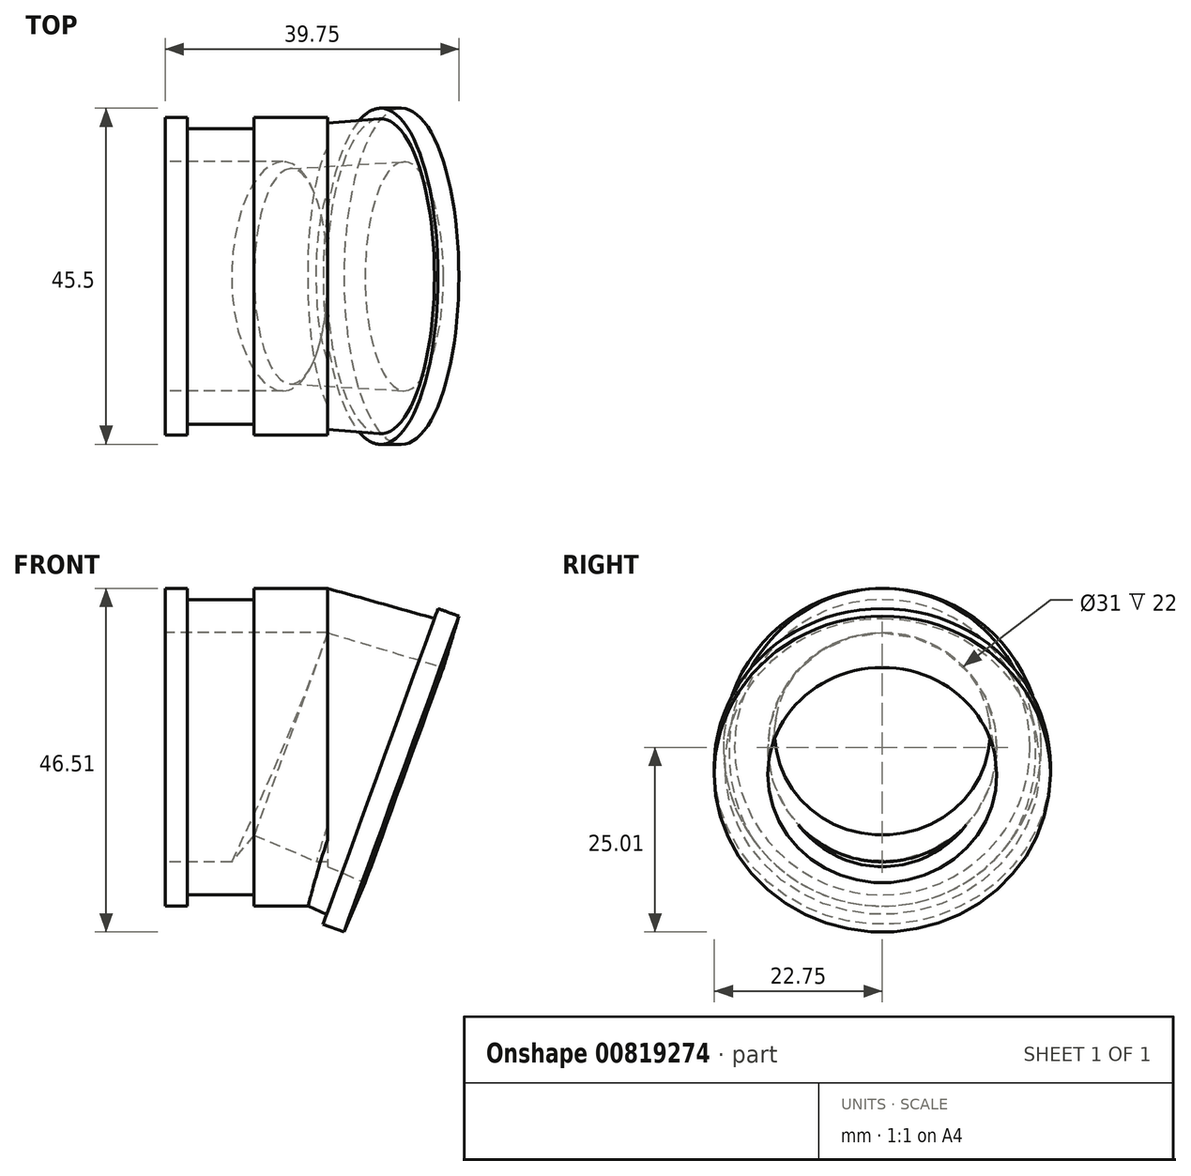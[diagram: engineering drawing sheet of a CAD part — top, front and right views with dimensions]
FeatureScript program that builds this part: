
annotation { "Feature Type Name" : "Feature", "Feature Type Description" : "" }
export const myFeature = defineFeature(function(context is Context, id is Id, definition is map)
    precondition{}
    {
        {
            var Q0;
            Q0=qCreatedBy(makeId("Front.planeOp"),FACE);
            var sketch = newSketch(context, id + "F0", { "sketchPlane" : qUnion([Q0])});
            skLineSegment(sketch, "E0", {"start": v(-22, 15.5) * mm, "end": v(-22, 21.5) * mm});
            skLineSegment(sketch, "E1", {"start": v(-22, 21.5) * mm, "end": v(-19, 21.5) * mm});
            skLineSegment(sketch, "E2", {"start": v(-19, 21.5) * mm, "end": v(-19, 20) * mm});
            skLineSegment(sketch, "E3", {"start": v(-19, 20) * mm, "end": v(-10, 20) * mm});
            skLineSegment(sketch, "E4", {"start": v(-10, 20) * mm, "end": v(-10, 21.5) * mm});
            skLineSegment(sketch, "E5", {"start": v(-10, 21.5) * mm, "end": v(0, 21.5) * mm});
            skLineSegment(sketch, "E6", {"start": v(0, 15.5) * mm, "end": v(-22, 15.5) * mm});
            skLineSegment(sketch, "E7", {"start": v(-22, 0) * mm, "end": v(0, 0) * mm, "construction": true});
            skLineSegment(sketch, "E8", {"start": v(0, 21.5) * mm, "end": v(0, 15.5) * mm});
            skSolve(sketch);
        }
        {
            var Q0;
            Q0=makeQuery(id+"F0.imprint","IMPRINT",FACE,{"disambiguationData":[TD([[makeQuery(id+"F0.imprint","IMPRINT",EDGE,{"derivedFrom":sQuery(id+"F0.wireOp",EDGE,"E0")}),-1.0]])]});
            var Q1;
            Q1=sQuery(id+"F0.wireOp",EDGE,"E7");
            revolve(context, id + "F1", {"surfaceOperationType" : NewSurfaceOperationType.NEW, "entities" : qUnion([Q0]), "axis" : qUnion([Q1]), "revolveType" : RevolveType.FULL});
        }
        {
            var Q0;
            Q0=qCreatedBy(makeId("Front.planeOp"),FACE);
            var sketch = newSketch(context, id + "F2", { "sketchPlane" : qUnion([Q0])});
            skLineSegment(sketch, "E9", {"start": v(0, 21.5) * mm, "end": v(14.44, 17.43) * mm});
            skLineSegment(sketch, "E10", {"start": v(14.44, 17.43) * mm, "end": v(14.93, 18.78) * mm});
            skLineSegment(sketch, "E11", {"start": v(14.93, 18.78) * mm, "end": v(17.75, 17.75) * mm});
            skLineSegment(sketch, "E12", {"start": v(17.75, 17.75) * mm, "end": v(15.66, 10.8) * mm});
            skLineSegment(sketch, "E13", {"start": v(15.66, 10.8) * mm, "end": v(0, 15.5) * mm});
            skLineSegment(sketch, "E14", {"start": v(0, 15.5) * mm, "end": v(0, 21.5) * mm});
            skLineSegment(sketch, "E15", {"start": v(0, 0) * mm, "end": v(27.21, -9.9) * mm, "construction": true});
            skSolve(sketch);
        }
        {
            var Q0;
            Q0=makeQuery(id+"F2.imprint","IMPRINT",FACE,{"disambiguationData":[TD([[makeQuery(id+"F2.imprint","IMPRINT",EDGE,{"derivedFrom":sQuery(id+"F2.wireOp",EDGE,"E9")}),-1.0]])]});
            var Q1;
            Q1=sQuery(id+"F2.wireOp",EDGE,"E15");
            revolve(context, id + "F3", {"operationType" : NewBodyOperationType.ADD, "surfaceOperationType" : NewSurfaceOperationType.NEW, "entities" : qUnion([Q0]), "axis" : qUnion([Q1]), "revolveType" : RevolveType.FULL});
        }
    });
